# Revit family: kawneer - 1600 powershade - aluminum_16445
name_source: partatom
category: Generic Models
revit_build: Autodesk Revit 2015 (Build: 20140905_0730(x64)
units: mm (PartAtom-declared; Revit-internal decimal feet)

## types (1)
- 96" Width (Max.)
    Assembly Code = B2020400
    Description = Architects and building owners are increasingly recognizing the need for "green" building products that conserve energy and enhance building performance without compromising aesthetics. Kawneer has responded to this challenge by designing 1600 PowerShade®, a BIPV (Building Integrated Photovoltaic) sunshade that generates solar power while also providing optimal shade in a total system/single source solution.
 
The result is a classically designed sunshade that conserves energy and reduces building operating costs. Fully tested and factory fabricated, this preengineered sunshade blends photovoltaic technology — amorphous silicon panels — with sleek design, easy installation and simple maintenance.
 
In addition, PowerShade® is engineered to meet rigorous structural loads while minimizing material requirements.
    Manufacturer = Kawneer
    Model = 1600 PowerShade® - Aluminum
    Outside Shade Width = 8' - 0"
    Product data url = https://bimobject.com
    Shade Finish = Kawneer - 1600 PowerShade
    Type Comments = Aluminum
    URL = http://www.kawneer.com

## geometry (parser evidence)
native form markers: Extrusion x15, Sweep x2
no freeform markers — native parametric forms only
